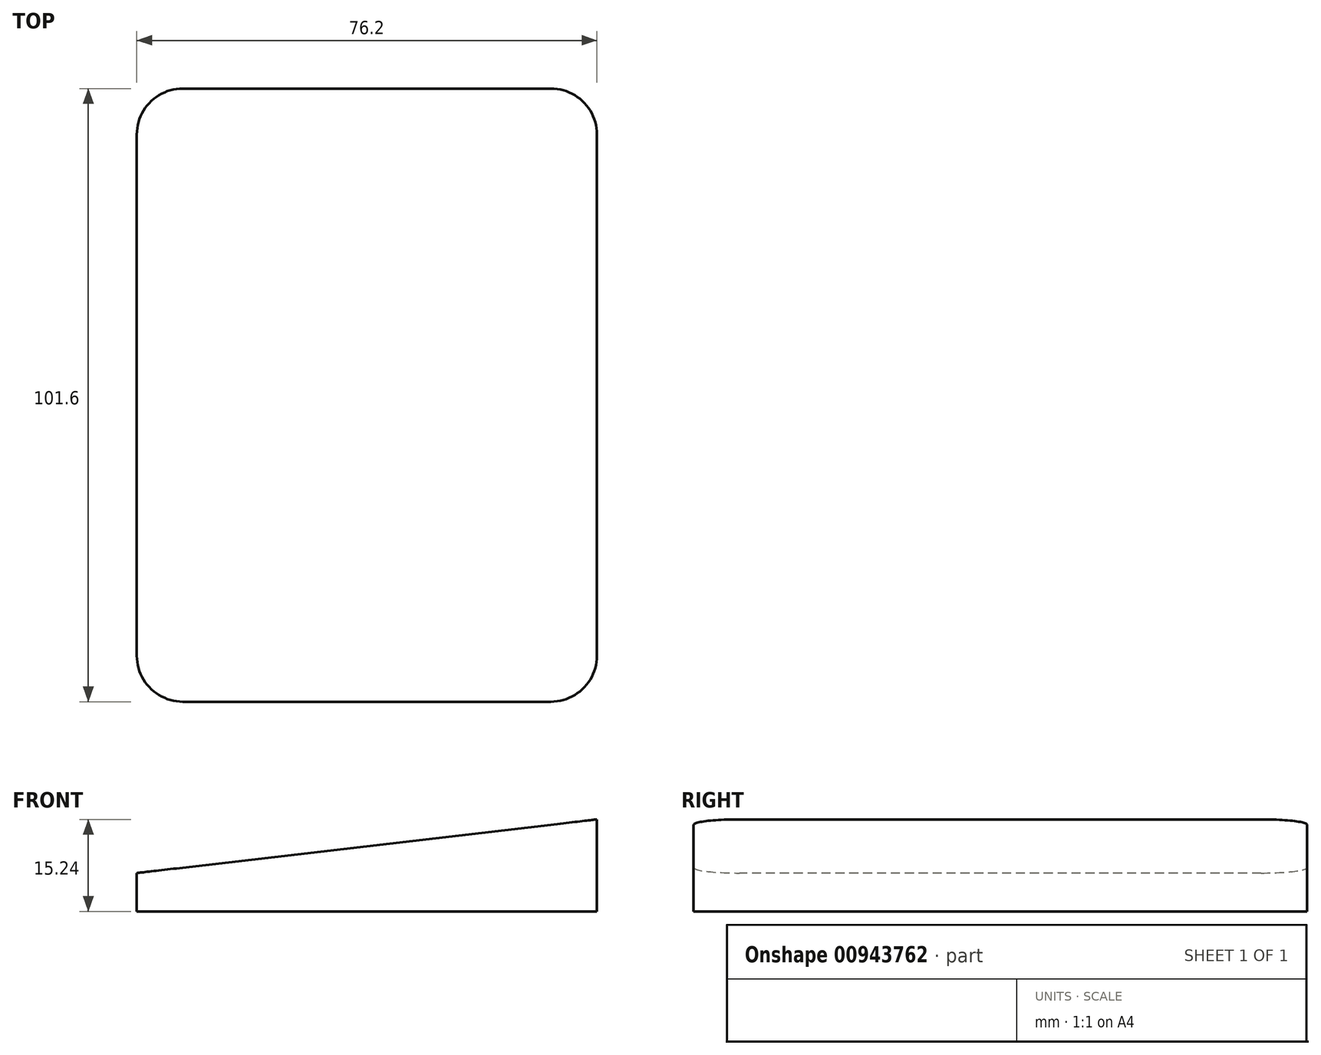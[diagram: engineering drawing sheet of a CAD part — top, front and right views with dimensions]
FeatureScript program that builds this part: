
annotation { "Feature Type Name" : "Feature", "Feature Type Description" : "" }
export const myFeature = defineFeature(function(context is Context, id is Id, definition is map)
    precondition{}
    {
        {
            var Q0;
            Q0=qCreatedBy(makeId("Front.planeOp"),FACE);
            cPlane(context, id + "F0", {"entities" : qUnion([Q0]), "cplaneType" : CPlaneType.OFFSET, "offset" : 254 * mm, "width" : 152.4 * mm, "height" : 152.4 * mm});
        }
        {
            var Q0;
            Q0=qCreatedBy(makeId("Top.planeOp"),FACE);
            var sketch = newSketch(context, id + "F1", { "sketchPlane" : qUnion([Q0])});
            skLineSegment(sketch, "E0.bottom", {"start": v(-30.48, 50.8) * mm, "end": v(30.48, 50.8) * mm});
            skLineSegment(sketch, "E0.top", {"start": v(-30.48, -50.8) * mm, "end": v(30.48, -50.8) * mm});
            skLineSegment(sketch, "E0.left", {"start": v(-38.1, 43.18) * mm, "end": v(-38.1, -43.18) * mm});
            skLineSegment(sketch, "E0.right", {"start": v(38.1, 43.18) * mm, "end": v(38.1, -43.18) * mm});
            skLineSegment(sketch, "E1", {"start": v(-38.1, 0) * mm, "end": v(38.1, 0) * mm, "construction": true});
            skLineSegment(sketch, "E2", {"start": v(0, 50.8) * mm, "end": v(0, -50.8) * mm, "construction": true});
            skPoint(sketch, "E3", {"position": v(0, 0) * mm});
            skPoint(sketch, "E4.visualSharp", {"position": v(-38.1, 50.8) * mm});
            skArc(sketch, "E4.filletArc", {"start": v(-30.48, 50.8) * mm, "mid": v(-35.87, 48.57) * mm, "end": v(-38.1, 43.18) * mm});
            skPoint(sketch, "E5.visualSharp", {"position": v(38.1, 50.8) * mm});
            skArc(sketch, "E5.filletArc", {"start": v(38.1, 43.18) * mm, "mid": v(35.87, 48.57) * mm, "end": v(30.48, 50.8) * mm});
            skPoint(sketch, "E6.visualSharp", {"position": v(-38.1, -50.8) * mm});
            skArc(sketch, "E6.filletArc", {"start": v(-38.1, -43.18) * mm, "mid": v(-35.87, -48.57) * mm, "end": v(-30.48, -50.8) * mm});
            skPoint(sketch, "E7.visualSharp", {"position": v(38.1, -50.8) * mm});
            skArc(sketch, "E7.filletArc", {"start": v(30.48, -50.8) * mm, "mid": v(35.87, -48.57) * mm, "end": v(38.1, -43.18) * mm});
            skSolve(sketch);
        }
        {
            var Q0;
            Q0=qCreatedBy(id+"F0.planeOp",FACE);
            var sketch = newSketch(context, id + "F2", { "sketchPlane" : qUnion([Q0])});
            skLineSegment(sketch, "E8", {"start": v(-38.1, 0) * mm, "end": v(-38.1, 6.35) * mm});
            skLineSegment(sketch, "E9", {"start": v(-38.1, 6.35) * mm, "end": v(38.1, 15.24) * mm});
            skLineSegment(sketch, "E10", {"start": v(38.1, 15.24) * mm, "end": v(38.1, 0) * mm});
            skLineSegment(sketch, "E11", {"start": v(38.1, 0) * mm, "end": v(-38.1, 0) * mm});
            skSolve(sketch);
        }
        {
            var Q0;
            Q0=makeQuery(id+"F1.imprint","IMPRINT",FACE,{"disambiguationData":[TD([[makeQuery(id+"F1.imprint","IMPRINT",EDGE,{"derivedFrom":sQuery(id+"F1.wireOp",EDGE,"E0.bottom")}),-1.0]])]});
            var Q1;
            Q1=sQuery(id+"F2.wireOp",VERTEX,"E9.end");
            extrude(context, id + "F3", {"entities" : qUnion([Q0]), "endBound" : BoundingType.UP_TO_VERTEX, "depth" : 15.24 * mm, "endBoundEntityVertex" : qUnion([Q1]), "offsetDistance" : 25.4 * mm});
        }
        {
            var Q0;
            Q0 = qSketchRegion(id + "F2", true);
            extrude(context, id + "F4", {"entities" : qUnion([Q0]), "operationType" : NewBodyOperationType.INTERSECT, "endBound" : BoundingType.THROUGH_ALL, "oppositeDirection" : true, "depth" : 101.6 * mm, "offsetDistance" : 25.4 * mm});
        }
    });
